# Revit family: ASL_64_Series_timber_door_40mm_jamb_1
name_source: partatom
category: Detail Items
revit_build: Autodesk Revit 2018 (Build: 20170223_1515(x64)
units: mm (PartAtom-declared; Revit-internal decimal feet)

## family parameters
Rotate with component = No
Section Shape = Not Defined
Shared = Yes

## types (4) — shared parameters
Manufacturer = Aluminate Solutions Limited
Technical Info = www.aluminate.nz

## per-type parameters (varying)
| type | Door Depth | Door Stop_40 | Door_40 | Flush Infill | Glazing | Headsection_ASL_405 | Headsection_ASL_546 | Raven Seal | Type Comments |
| Double Action Door 40mm | 19 mm  [stored 0.062336 ft] | No | Yes | Yes | No | No | Yes | No | ASL 64 Series Jamb 1 With Double Action 40mm Timber Door |
| Single Action Door 40mm | 47 mm  [stored 0.154199 ft] | Yes | Yes | No | No | No | Yes | No | ASL 64 Series Jamb 1 With Single Action 40mm Timber Door |
| Single Action Raven Seal Door 40mm | 51 mm  [stored 0.167323 ft] | No | Yes | No | No | Yes | No | Yes | ASL 64 Series Jamb 1 With Single Raven Seal Action 40mm Timber Door |
| Glazing | 19 mm  [stored 0.062336 ft] | No | No | No | Yes | No | Yes | No | ASL 64 Series Jamb 1 With Glazing |

note: [stored X ft] marks values corroborated as IEEE doubles in the binary element streams (Revit-internal decimal feet)

## geometry (parser evidence)
native form markers: Sweep x8
no freeform markers — native parametric forms only
